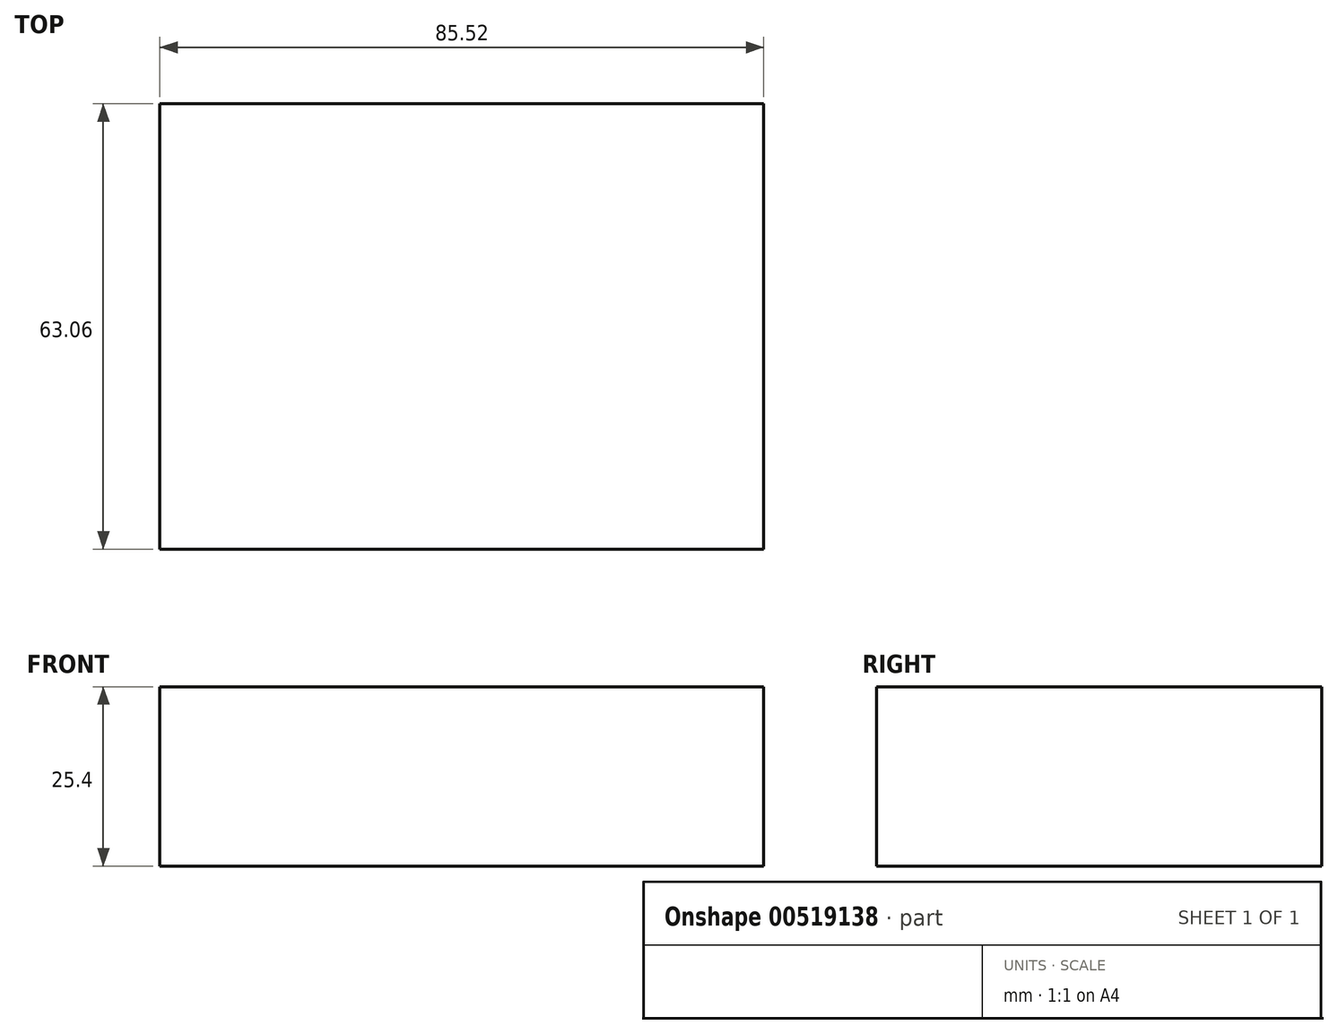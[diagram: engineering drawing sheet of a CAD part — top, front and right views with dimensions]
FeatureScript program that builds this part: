
annotation { "Feature Type Name" : "Feature", "Feature Type Description" : "" }
export const myFeature = defineFeature(function(context is Context, id is Id, definition is map)
    precondition{}
    {
        {
            var Q0;
            Q0=qCreatedBy(makeId("Top.planeOp"),FACE);
            var sketch = newSketch(context, id + "F0", { "sketchPlane" : qUnion([Q0])});
            skLineSegment(sketch, "E0.bottom", {"start": v(42.76, 31.53) * mm, "end": v(-42.76, 31.53) * mm});
            skLineSegment(sketch, "E0.top", {"start": v(42.76, -31.53) * mm, "end": v(-42.76, -31.53) * mm});
            skLineSegment(sketch, "E0.left", {"start": v(42.76, 31.53) * mm, "end": v(42.76, -31.53) * mm});
            skLineSegment(sketch, "E0.right", {"start": v(-42.76, 31.53) * mm, "end": v(-42.76, -31.53) * mm});
            skPoint(sketch, "E0.middle", {"position": v(0, 0) * mm});
            skSolve(sketch);
        }
        {
            var Q0;
            Q0 = qSketchRegion(id + "F0", true);
            extrude(context, id + "F1", {"entities" : qUnion([Q0]), "depth" : 25.4 * mm});
        }
    });
